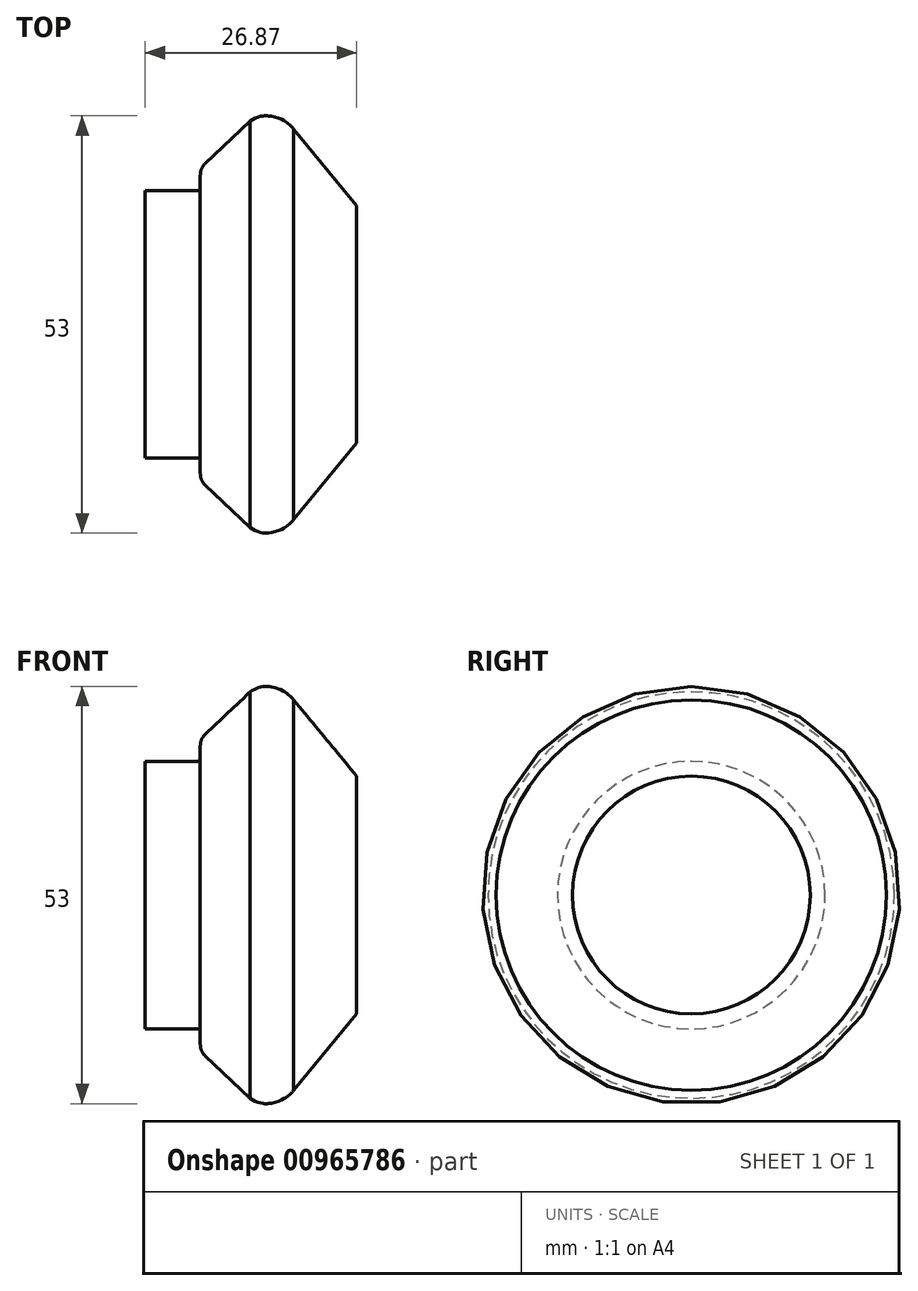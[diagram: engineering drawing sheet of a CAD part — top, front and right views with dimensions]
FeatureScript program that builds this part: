
annotation { "Feature Type Name" : "Feature", "Feature Type Description" : "" }
export const myFeature = defineFeature(function(context is Context, id is Id, definition is map)
    precondition{}
    {
        {
            var Q0;
            Q0=qCreatedBy(makeId("Front.planeOp"),FACE);
            var sketch = newSketch(context, id + "F0", { "sketchPlane" : qUnion([Q0])});
            skLineSegment(sketch, "E0", {"start": v(9.87, 24.79) * mm, "end": v(17.87, 15.1) * mm});
            skFitSpline(sketch, "E1", {"points": [v(3.84, 25.48) * mm, v(5.4, 26.36) * mm, v(6.9, 26.46) * mm, v(8.5, 25.94) * mm, v(9.63, 25.07) * mm, v(9.87, 24.79) * mm], "startDerivative": vector(6.57, 4.44) * mm, "endDerivative": vector(1.73, -2.25) * mm});
            skLineSegment(sketch, "E2", {"start": v(-2, 0) * mm, "end": v(-9, 0) * mm});
            skLineSegment(sketch, "E3", {"start": v(-2, 0) * mm, "end": v(17.87, 0) * mm});
            skLineSegment(sketch, "E4", {"start": v(17.87, 15.1) * mm, "end": v(17.87, 0) * mm});
            skPoint(sketch, "E5.visualSharp", {"position": v(-2, 16) * mm});
            skLineSegment(sketch, "E6", {"start": v(-1.37, 20.43) * mm, "end": v(4.36, 25.83) * mm});
            skPoint(sketch, "E7.visualSharp", {"position": v(-2, 19.84) * mm});
            skArc(sketch, "E7.filletArc", {"start": v(-1.37, 20.43) * mm, "mid": v(-1.84, 19.77) * mm, "end": v(-2, 18.97) * mm});
            skLineSegment(sketch, "E8", {"start": v(-9, 0) * mm, "end": v(-9, 17) * mm});
            skLineSegment(sketch, "E9", {"start": v(-9, 17) * mm, "end": v(-2.34, 17) * mm});
            skLineSegment(sketch, "E10", {"start": v(-2, 17.34) * mm, "end": v(-2, 18.97) * mm});
            skPoint(sketch, "E11.visualSharp", {"position": v(-2, 17) * mm});
            skArc(sketch, "E11.filletArc", {"start": v(-2.34, 17) * mm, "mid": v(-2.1, 17.1) * mm, "end": v(-2, 17.34) * mm});
            skSolve(sketch);
        }
        {
            var Q0;
            {var subQ4=sQuery(id+"F0.wireOp",EDGE,"E0");Q0=makeQuery(id+"F0.imprint","IMPRINT",FACE,{"disambiguationData":[TD([[makeQuery(id+"F0.imprint","IMPRINT",EDGE,{"derivedFrom":subQ4}),-1.0]])]});}
            var Q1;
            Q1=sQuery(id+"F0.wireOp",EDGE,"E3");
            revolve(context, id + "F1", {"surfaceOperationType" : NewSurfaceOperationType.NEW, "entities" : qUnion([Q0]), "axis" : qUnion([Q1]), "revolveType" : RevolveType.FULL});
        }
    });
